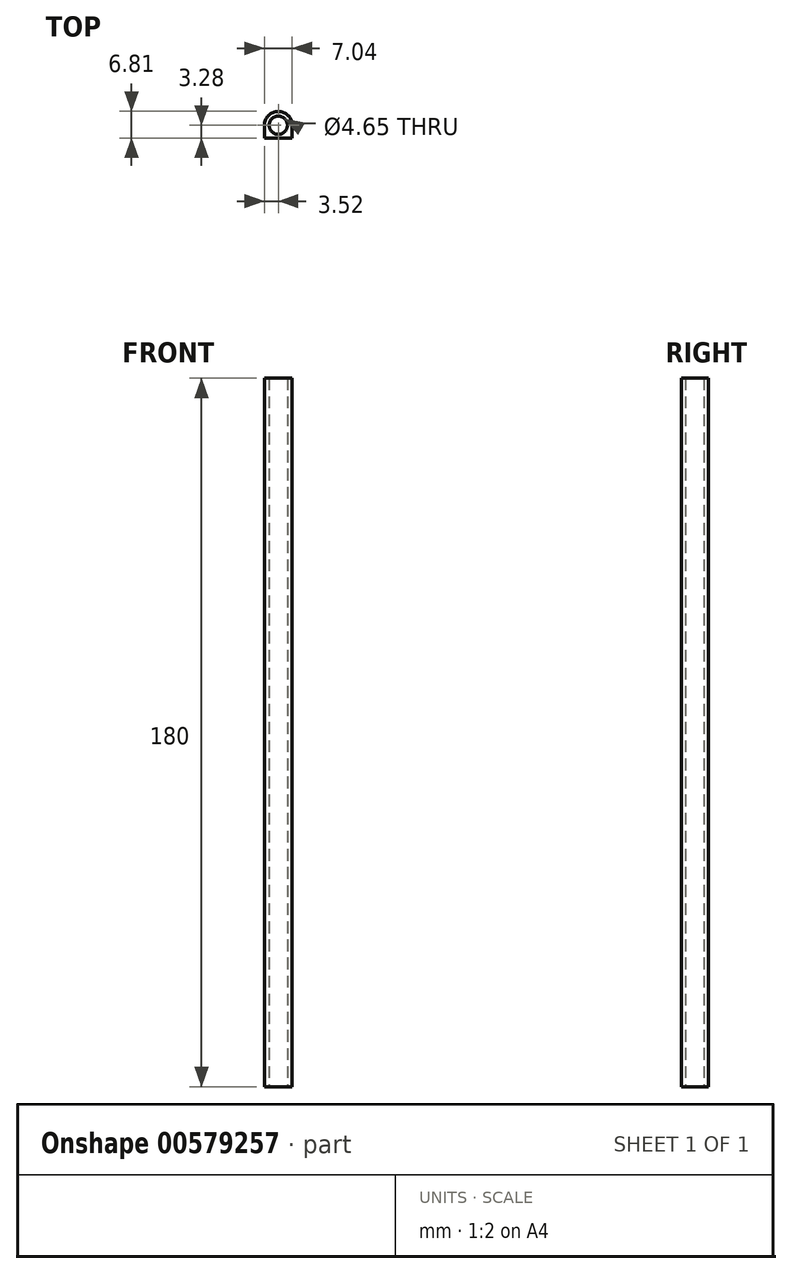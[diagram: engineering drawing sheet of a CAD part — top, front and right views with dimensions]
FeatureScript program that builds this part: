
annotation { "Feature Type Name" : "Feature", "Feature Type Description" : "" }
export const myFeature = defineFeature(function(context is Context, id is Id, definition is map)
    precondition{}
    {
        {
            var Q0;
            Q0=qCreatedBy(makeId("Top.planeOp"),FACE);
            var sketch = newSketch(context, id + "F0", { "sketchPlane" : qUnion([Q0])});
            skCircle(sketch, "E0", {"center": v(0, 0) * mm, "radius": 2.33 * mm});
            skLineSegment(sketch, "E1.top", {"start": v(-3.52, -3.27) * mm, "end": v(3.53, -3.28) * mm});
            skLineSegment(sketch, "E1.left", {"start": v(-3.52, 0) * mm, "end": v(-3.52, -3.28) * mm});
            skLineSegment(sketch, "E1.right", {"start": v(3.52, 0) * mm, "end": v(3.52, -3.28) * mm});
            skArc(sketch, "E2", {"start": v(3.53, 0) * mm, "mid": v(0, 3.52) * mm, "end": v(-3.52, 0) * mm});
            skSolve(sketch);
        }
        {
            var Q0;
            Q0=makeQuery(id+"F0.imprint","IMPRINT",FACE,{"disambiguationData":[TD([[makeQuery(id+"F0.imprint","IMPRINT",EDGE,{"derivedFrom":sQuery(id+"F0.wireOp",EDGE,"E0")}),-1.0]])]});
            extrude(context, id + "F1", {"entities" : qUnion([Q0]), "depth" : 180 * mm, "offsetDistance" : 25 * mm});
        }
    });
